# Revit family: MB177EM_TEU
name_source: partatom
category: Plumbing Fixtures
revit_build: Autodesk Revit 2018 (Build: 20170223_1515(x64)
units: mm (PartAtom-declared; Revit-internal decimal feet)

## family parameters
Always vertical = Yes
Cut with Voids When Loaded = No
OmniClass Number = 23.45.00.00
OmniClass Title = Sanitary, Laundry, and Cleaning Equipment
Part Type = Normal
Room Calculation Point = No
Round Connector Dimension = Use Diameter
Shared = No
Work Plane-Based = No

## types (1)
- MB177EM_TEU
    CW Connection = No
    Description = Push plate
    Finish = <By Category>
    HW Connection = No
    Height = 152 mm  [stored 0.498688 ft]
    Length = 6 mm  [stored 0.019685 ft]
    Manufacturer = TOTO LTD.
    Material = Plastic
    Model = MB177EM#S
    Seat Included = No
    URL = https://eu.toto.com
    Vent Connection = No
    Waste Connection = No
    Width = 235 mm  [stored 0.770997 ft]

note: [stored X ft] marks values corroborated as IEEE doubles in the binary element streams (Revit-internal decimal feet)

## geometry (parser evidence)
native form markers: Sweep x2
no freeform markers — native parametric forms only
